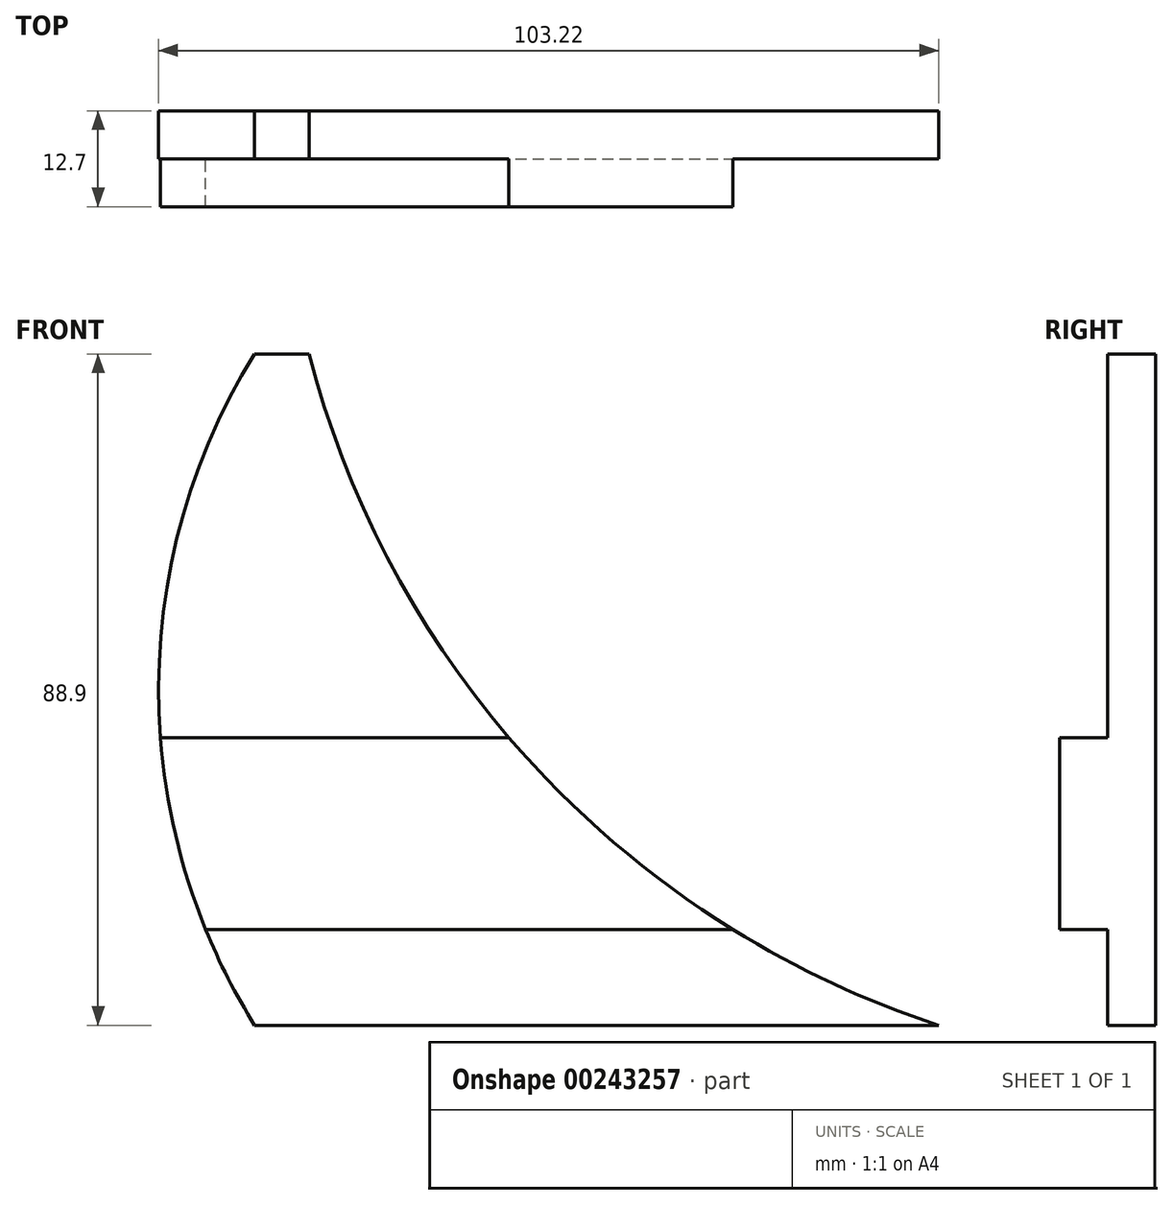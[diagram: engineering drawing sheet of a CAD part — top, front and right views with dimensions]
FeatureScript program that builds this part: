
annotation { "Feature Type Name" : "Feature", "Feature Type Description" : "" }
export const myFeature = defineFeature(function(context is Context, id is Id, definition is map)
    precondition{}
    {
        {
            var Q0;
            Q0=qCreatedBy(makeId("Front.planeOp"),FACE);
            var sketch = newSketch(context, id + "F0", { "sketchPlane" : qUnion([Q0])});
            skLineSegment(sketch, "E0", {"start": v(0, 0) * mm, "end": v(0, -88.9) * mm});
            skLineSegment(sketch, "E1", {"start": v(0, -88.9) * mm, "end": v(104.78, -88.9) * mm});
            skLineSegment(sketch, "E2", {"start": v(104.78, -88.9) * mm, "end": v(104.78, 0) * mm});
            skLineSegment(sketch, "E3", {"start": v(104.77, 0) * mm, "end": v(0, 0) * mm});
            skLineSegment(sketch, "E4", {"start": v(104.78, 0) * mm, "end": v(104.78, 31.75) * mm, "construction": true});
            skLineSegment(sketch, "E5", {"start": v(13.01, -88.9) * mm, "end": v(104.78, -88.9) * mm});
            skLineSegment(sketch, "E6", {"start": v(187.27, 31.75) * mm, "end": v(-39.47, 31.75) * mm, "construction": true});
            skLineSegment(sketch, "E7", {"start": v(142.88, 72.94) * mm, "end": v(142.88, -111.59) * mm, "construction": true});
            skCircle(sketch, "E8", {"center": v(142.88, 31.75) * mm, "radius": 127 * mm});
            skCircle(sketch, "E9", {"center": v(84.14, -44.45) * mm, "radius": 84.14 * mm});
            skLineSegment(sketch, "E10", {"start": v(6.22, -76.2) * mm, "end": v(75.97, -76.2) * mm});
            skLineSegment(sketch, "E11", {"start": v(0.24, -50.8) * mm, "end": v(46.36, -50.8) * mm});
            skPoint(sketch, "E12", {"position": v(12.7, 0) * mm});
            skPoint(sketch, "E13", {"position": v(19.9, 0) * mm});
            skSolve(sketch);
        }
        {
            var Q0;
            {var subQ0=sQuery(id+"F0.wireOp",EDGE,"E11");Q0=makeQuery(id+"F0.imprint","IMPRINT",FACE,{"disambiguationData":[TD([[makeQuery(id+"F0.imprint","IMPRINT",EDGE,{"derivedFrom":subQ0}),1.0]])]});}
            var Q1;
            {var subQ0=sQuery(id+"F0.wireOp",EDGE,"E10");Q1=makeQuery(id+"F0.imprint","IMPRINT",FACE,{"disambiguationData":[TD([[makeQuery(id+"F0.imprint","IMPRINT",EDGE,{"derivedFrom":subQ0}),1.0]])]});}
            var Q2;
            {var subQ0=sQuery(id+"F0.wireOp",EDGE,"E10");Q2=makeQuery(id+"F0.imprint","IMPRINT",FACE,{"disambiguationData":[TD([[makeQuery(id+"F0.imprint","IMPRINT",EDGE,{"derivedFrom":subQ0}),-1.0]])]});}
            extrude(context, id + "F1", {"entities" : qUnion([Q0, Q1, Q2]), "depth" : 6.35 * mm});
        }
        {
            var Q0;
            Q0=makeQuery(id+"F1.opExtrude","CAP_FACE",FACE,{"disambiguationData":[OSD([sQuery(id+"F0.wireOp",EDGE,"E1"),sQuery(id+"F0.wireOp",EDGE,"E3"),sQuery(id+"F0.wireOp",EDGE,"E5"),sQuery(id+"F0.wireOp",EDGE,"E8"),sQuery(id+"F0.wireOp",EDGE,"E9")])],"isStart":false});
            var sketch = newSketch(context, id + "F2", { "sketchPlane" : qUnion([Q0])});
            skLineSegment(sketch, "E14", {"start": v(6.22, -76.2) * mm, "end": v(75.97, -76.2) * mm});
            skLineSegment(sketch, "E15", {"start": v(0.24, -50.8) * mm, "end": v(46.36, -50.8) * mm});
            skLineSegment(sketch, "E16", {"start": v(29.46, -25.4) * mm, "end": v(2.18, -25.4) * mm});
            skSolve(sketch);
        }
        {
            var Q0;
            {var subQ0=sQuery(id+"F2.wireOp",EDGE,"E14");Q0=makeQuery(id+"F2.imprint","IMPRINT",FACE,{"disambiguationData":[TD([[makeQuery(id+"F2.imprint","IMPRINT",EDGE,{"derivedFrom":subQ0}),1.0]])]});}
            extrude(context, id + "F3", {"entities" : qUnion([Q0]), "operationType" : NewBodyOperationType.ADD, "depth" : 6.35 * mm});
        }
    });
